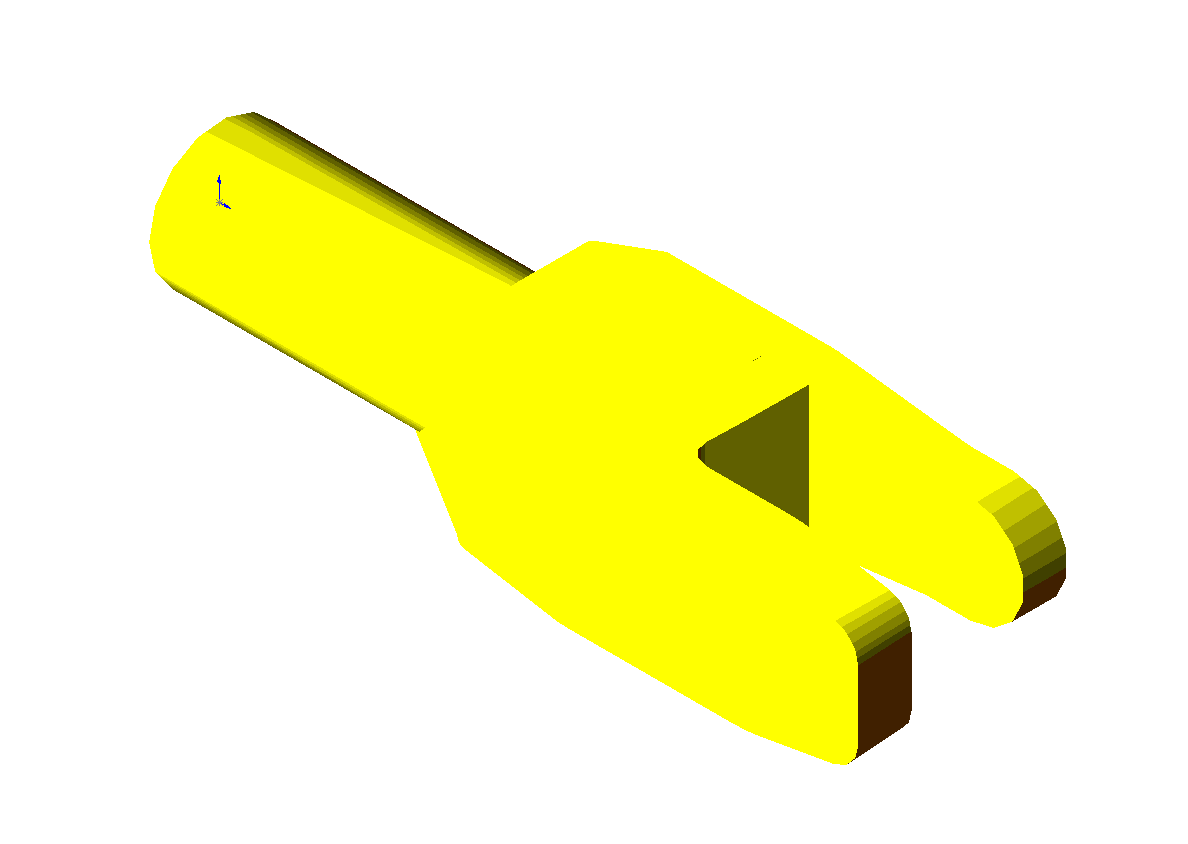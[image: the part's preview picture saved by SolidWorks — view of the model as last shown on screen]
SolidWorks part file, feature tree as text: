
SOLIDWORKS PART (.sldprt)
format: sldprt  version: not decoded by parser v0  size: 222,720 bytes
history: native  units: mm
features: sketch x7, extrude x5, plane x4, cut_extrude x2, material x1 (+9 scaffold rows collapsed)
feature tree (28):
  scaffold x9  (default folders/planes/origin — collapsed)
  material  "Material <not specified>"
  plane  "FRONT"
  plane  "TOP"
  plane  "SIDE"
  sketch  "Sketch5"  dims[D1=93.726mm]
  extrude  "Base-Extrude"  Depth=353.695mm
  sketch  "Sketch6"  dims[D1=4.24mm]
  extrude  "Boss-Extrude1"  Depth=78.105mm
  sketch  "Sketch8"
  cut_extrude  "Cut-Extrude1"  Depth=61.595mm
  sketch  "Sketch9"
  extrude  "Boss-Extrude2"  Depth=29.21mm
  sketch  "Sketch10"
  cut_extrude  "Cut-Extrude2"  [1 undecoded]
  sketch  "Sketch11"
  extrude  "Boss-Extrude3"  Depth=44.45mm
  plane  "Plane1"
  sketch  "Sketch12"
  extrude  "Boss-Extrude4"  Depth=44.45mm
decode coverage: 8 of 14 modeling features carry decoded parameters
note: 1 parameter value undecoded
note: suppression state not decoded; provenance and decode notes live in map.json
